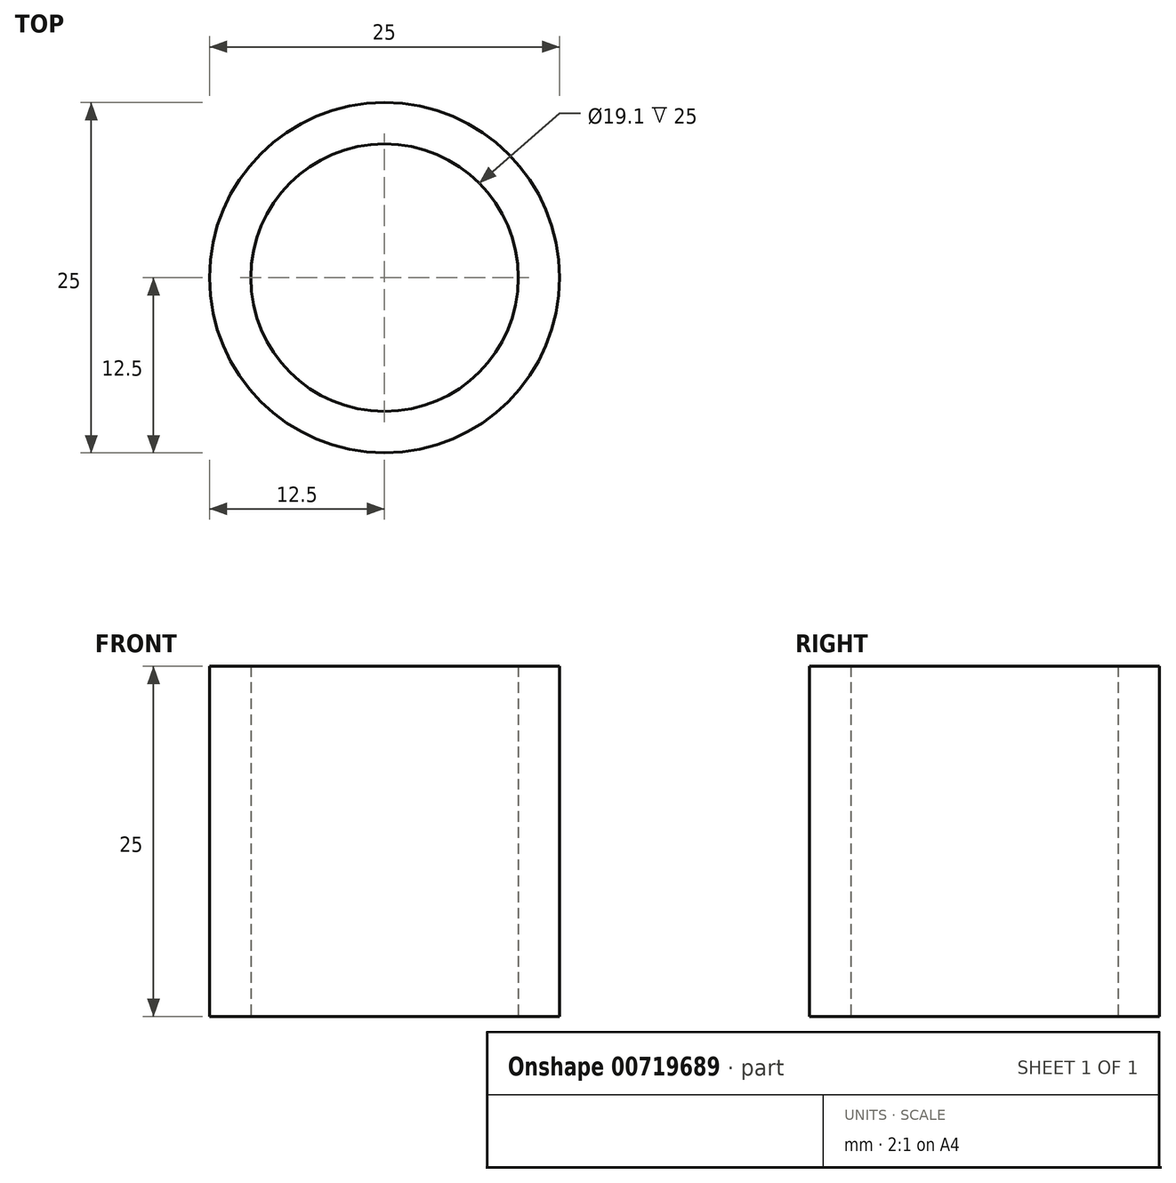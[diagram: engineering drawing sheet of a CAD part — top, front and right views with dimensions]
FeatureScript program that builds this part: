
annotation { "Feature Type Name" : "Feature", "Feature Type Description" : "" }
export const myFeature = defineFeature(function(context is Context, id is Id, definition is map)
    precondition{}
    {
        {
            var Q0;
            Q0=qCreatedBy(makeId("Top.planeOp"),FACE);
            var sketch = newSketch(context, id + "F0", { "sketchPlane" : qUnion([Q0])});
            skCircle(sketch, "E0", {"center": v(0, 0) * mm, "radius": 12.5 * mm});
            skCircle(sketch, "E1", {"center": v(0, 0) * mm, "radius": 9.55 * mm});
            skSolve(sketch);
        }
        {
            var Q0;
            Q0 = qSketchRegion(id + "F0", true);
            extrude(context, id + "F1", {"entities" : qUnion([Q0]), "depth" : 25 * mm, "offsetDistance" : 25 * mm});
        }
    });
